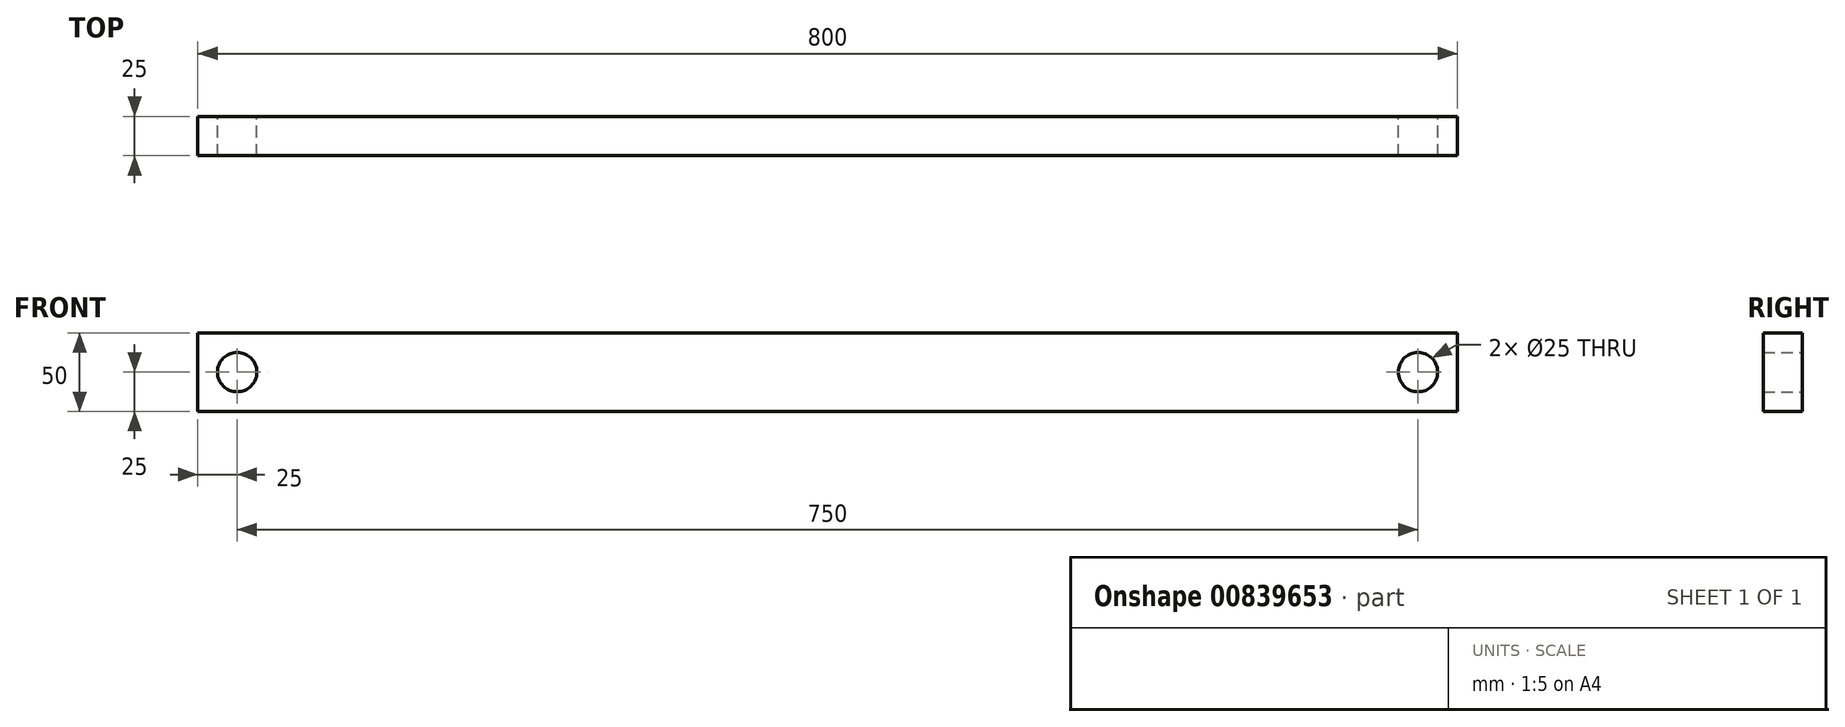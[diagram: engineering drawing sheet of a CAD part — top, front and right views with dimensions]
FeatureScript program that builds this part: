
annotation { "Feature Type Name" : "Feature", "Feature Type Description" : "" }
export const myFeature = defineFeature(function(context is Context, id is Id, definition is map)
    precondition{}
    {
        {
            var Q0;
            Q0=qCreatedBy(makeId("Front.planeOp"),FACE);
            var sketch = newSketch(context, id + "F0", { "sketchPlane" : qUnion([Q0])});
            skCircle(sketch, "E0", {"center": v(-375, 0) * mm, "radius": 12.5 * mm});
            skCircle(sketch, "E1", {"center": v(375, 0) * mm, "radius": 12.5 * mm});
            skLineSegment(sketch, "E2", {"start": v(-375, 0) * mm, "end": v(375, 0) * mm, "construction": true});
            skPoint(sketch, "E3", {"position": v(0, 0) * mm});
            skLineSegment(sketch, "E4.bottom", {"start": v(-400, 25) * mm, "end": v(400, 25) * mm});
            skLineSegment(sketch, "E4.top", {"start": v(-400, -25) * mm, "end": v(400, -25) * mm});
            skLineSegment(sketch, "E4.left", {"start": v(-400, 25) * mm, "end": v(-400, -25) * mm});
            skLineSegment(sketch, "E4.right", {"start": v(400, 25) * mm, "end": v(400, -25) * mm});
            skLineSegment(sketch, "E5", {"start": v(375, 0) * mm, "end": v(400, 25) * mm, "construction": true});
            skLineSegment(sketch, "E6", {"start": v(375, 0) * mm, "end": v(400, -25) * mm, "construction": true});
            skLineSegment(sketch, "E7", {"start": v(-375, 0) * mm, "end": v(-400, 25) * mm, "construction": true});
            skLineSegment(sketch, "E8", {"start": v(-375, 0) * mm, "end": v(-400, -25) * mm, "construction": true});
            skSolve(sketch);
        }
        {
            var Q0;
            Q0=makeQuery(id+"F0.imprint","IMPRINT",FACE,{"disambiguationData":[TD([[makeQuery(id+"F0.imprint","IMPRINT",EDGE,{"derivedFrom":sQuery(id+"F0.wireOp",EDGE,"E0")}),-1.0]])]});
            extrude(context, id + "F1", {"entities" : qUnion([Q0]), "depth" : 25 * mm, "offsetDistance" : 25 * mm});
        }
    });
